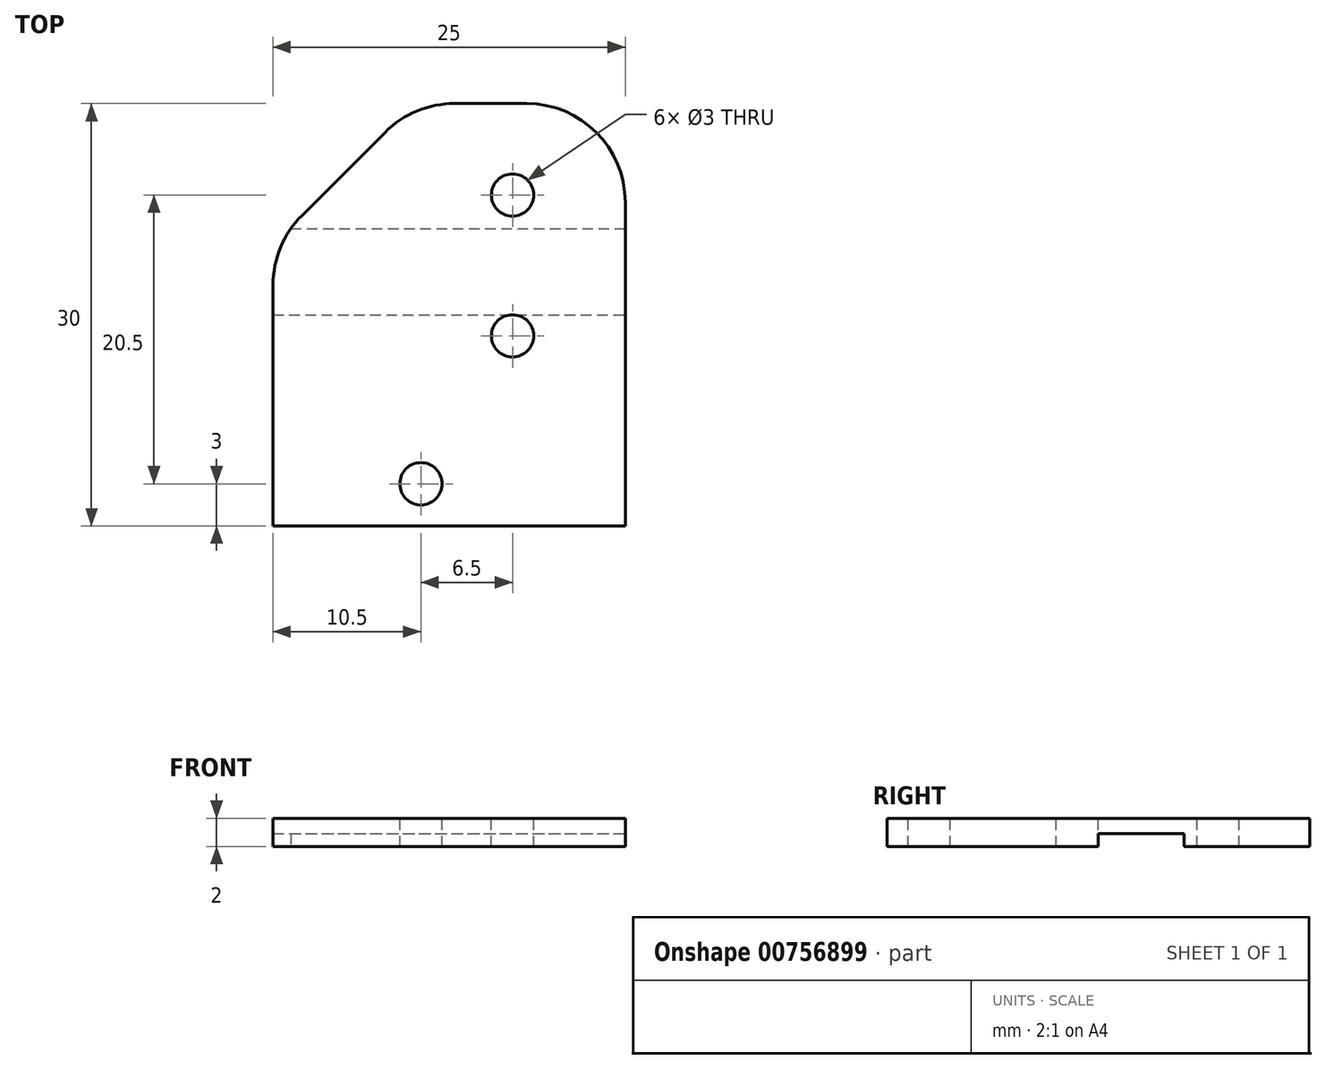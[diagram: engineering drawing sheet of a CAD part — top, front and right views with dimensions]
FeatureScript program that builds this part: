
annotation { "Feature Type Name" : "Feature", "Feature Type Description" : "" }
export const myFeature = defineFeature(function(context is Context, id is Id, definition is map)
    precondition{}
    {
        {
            var Q0;
            Q0=qCreatedBy(makeId("Top.planeOp"),FACE);
            var sketch = newSketch(context, id + "F0", { "sketchPlane" : qUnion([Q0])});
            skLineSegment(sketch, "E0.bottom", {"start": v(12.5, -15) * mm, "end": v(-12.5, -15) * mm});
            skLineSegment(sketch, "E0.top", {"start": v(12.5, 15) * mm, "end": v(-12.5, 15) * mm});
            skLineSegment(sketch, "E0.left", {"start": v(12.5, -15) * mm, "end": v(12.5, 15) * mm});
            skLineSegment(sketch, "E0.right", {"start": v(-12.5, -15) * mm, "end": v(-12.5, 15) * mm});
            skPoint(sketch, "E0.middle", {"position": v(0, 0) * mm});
            skSolve(sketch);
        }
        {
            var Q0;
            Q0=makeQuery(id+"F0.imprint","IMPRINT",FACE,{"disambiguationData":[TD([[makeQuery(id+"F0.imprint","IMPRINT",EDGE,{"derivedFrom":sQuery(id+"F0.wireOp",EDGE,"E0.bottom")}),-1.0]])]});
            extrude(context, id + "F1", {"entities" : qUnion([Q0]), "depth" : 2 * mm, "offsetDistance" : 25 * mm});
        }
        {
            var Q0;
            Q0=makeQuery(id+"F1.opExtrude","CAP_FACE",FACE,{"disambiguationData":[OSD([sQuery(id+"F0.wireOp",EDGE,"E0.bottom"),sQuery(id+"F0.wireOp",EDGE,"E0.top"),sQuery(id+"F0.wireOp",EDGE,"E0.left"),sQuery(id+"F0.wireOp",EDGE,"E0.right")])],"isStart":false});
            var sketch = newSketch(context, id + "F2", { "sketchPlane" : qUnion([Q0])});
            skCircle(sketch, "E1", {"center": v(-2, -12) * mm, "radius": 1.5 * mm});
            skPoint(sketch, "E1.centerSnap0", {"position": v(0, -15) * mm});
            skCircle(sketch, "E2", {"center": v(4.5, -1.5) * mm, "radius": 1.5 * mm});
            skCircle(sketch, "E3", {"center": v(4.5, 8.5) * mm, "radius": 1.5 * mm});
            skSolve(sketch);
        }
        {
            var Q0;
            Q0=qSketchRegion(id+"F2",true);
            extrude(context, id + "F3", {"entities" : qUnion([Q0]), "operationType" : NewBodyOperationType.REMOVE, "endBound" : BoundingType.THROUGH_ALL, "oppositeDirection" : true, "depth" : 25 * mm, "offsetDistance" : 25 * mm});
        }
        {
            var Q0;
            Q0=makeQuery(id+"F1.opExtrude","CAP_FACE",FACE,{"disambiguationData":[OSD([sQuery(id+"F0.wireOp",EDGE,"E0.bottom"),sQuery(id+"F0.wireOp",EDGE,"E0.top"),sQuery(id+"F0.wireOp",EDGE,"E0.left"),sQuery(id+"F0.wireOp",EDGE,"E0.right")])],"isStart":true});
            var sketch = newSketch(context, id + "F4", { "sketchPlane" : qUnion([Q0])});
            skLineSegment(sketch, "E4.bottom", {"start": v(-12.5, 0) * mm, "end": v(12.5, 0) * mm});
            skLineSegment(sketch, "E4.top", {"start": v(-12.5, -6.1) * mm, "end": v(12.5, -6.1) * mm});
            skLineSegment(sketch, "E4.left", {"start": v(-12.5, 0) * mm, "end": v(-12.5, -6.1) * mm});
            skLineSegment(sketch, "E4.right", {"start": v(12.5, 0) * mm, "end": v(12.5, -6.1) * mm});
            skPoint(sketch, "E4.middle", {"position": v(0, -3.05) * mm});
            skSolve(sketch);
        }
        {
            var Q0;
            Q0=qSketchRegion(id+"F4",true);
            extrude(context, id + "F5", {"entities" : qUnion([Q0]), "operationType" : NewBodyOperationType.REMOVE, "oppositeDirection" : true, "depth" : 0.9 * mm, "offsetDistance" : 25 * mm});
        }
        {
            var Q0;
            Q0=makeQuery(id+"F1.opExtrude","SWEPT_EDGE",EDGE,{"disambiguationData":[OSD([sQuery(id+"F0.wireOp",EDGE,"E0.top"),sQuery(id+"F0.wireOp",EDGE,"E0.right")])]});
            chamfer(context, id + "F6", {"entities" : qUnion([Q0]), "width" : 10 * mm, "tangentPropagation" : true});
        }
        {
            var Q0;
            {var subQ0=sQuery(id+"F0.wireOp",EDGE,"E0.right");Q0=makeQuery(id+"F6.opChamfer","BLEND_EDGE",EDGE,{"blendedFrom":[makeQuery(id+"F1.opExtrude","SWEPT_EDGE",EDGE,{"disambiguationData":[OSD([sQuery(id+"F0.wireOp",EDGE,"E0.top"),subQ0])]}),makeQuery(id+"F1.opExtrude","SWEPT_FACE",FACE,{"disambiguationData":[OSD([subQ0])]})],"blendedInto":[makeQuery(id+"F1.opExtrude","SWEPT_FACE",FACE,{"disambiguationData":[OSD([subQ0])]})]});}
            var Q1;
            {var subQ0=sQuery(id+"F0.wireOp",EDGE,"E0.top");Q1=makeQuery(id+"F6.opChamfer","BLEND_EDGE",EDGE,{"blendedFrom":[makeQuery(id+"F1.opExtrude","SWEPT_EDGE",EDGE,{"disambiguationData":[OSD([subQ0,sQuery(id+"F0.wireOp",EDGE,"E0.right")])]}),makeQuery(id+"F1.opExtrude","SWEPT_FACE",FACE,{"disambiguationData":[OSD([subQ0])]})],"blendedInto":[makeQuery(id+"F1.opExtrude","SWEPT_FACE",FACE,{"disambiguationData":[OSD([subQ0])]})]});}
            var Q2;
            Q2=makeQuery(id+"F1.opExtrude","SWEPT_EDGE",EDGE,{"disambiguationData":[OSD([sQuery(id+"F0.wireOp",EDGE,"E0.top"),sQuery(id+"F0.wireOp",EDGE,"E0.left")])]});
            fillet(context, id + "F7", {"entities" : qUnion([Q0, Q1, Q2]), "radius" : 7 * mm, "tangentPropagation" : true, "allowEdgeOverflow" : false});
        }
    });
